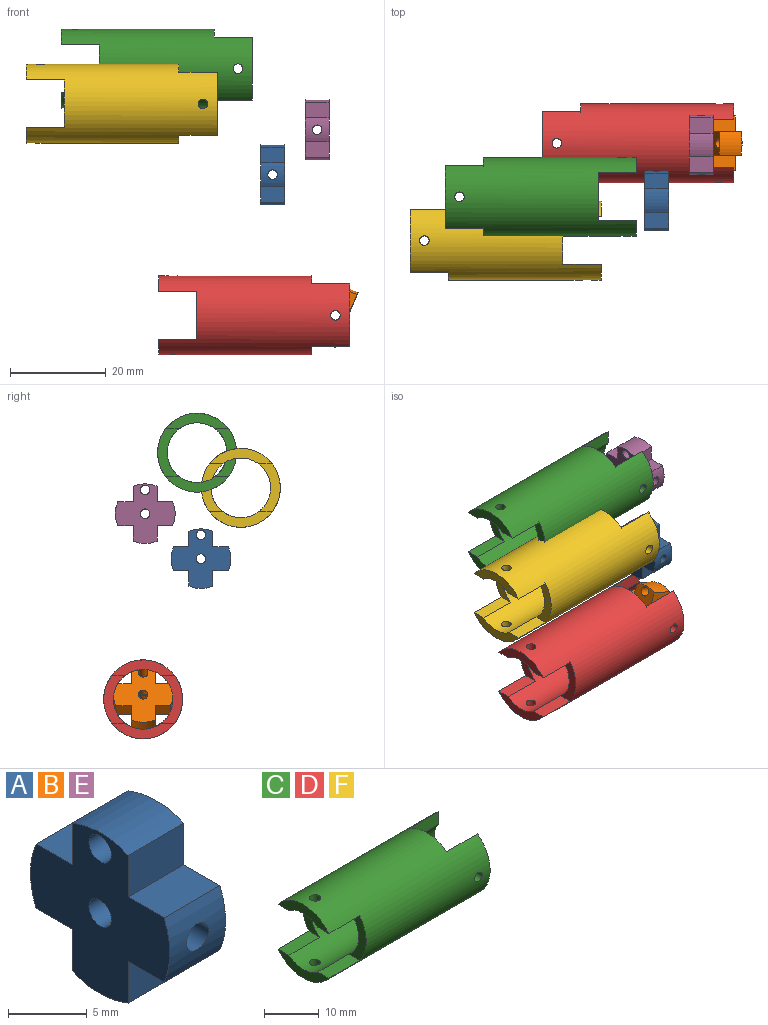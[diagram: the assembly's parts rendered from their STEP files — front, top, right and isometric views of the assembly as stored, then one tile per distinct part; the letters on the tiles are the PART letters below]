
ASSEMBLY  parts=6 mates=1
PART A: 19 faces, bbox 5x12.5x12.5 mm
  f0: cylinder r=1mm len=2.5mm, axis (-1,0,0), area 11.7mm2, adj f15,f17,f18
  f1: plane 5x3.23mm, normal (0,0,-1), area 16.1mm2, adj f2,f14,f15,f16
  f2: cylinder r=6.25mm len=5mm, axis (-1,0,0), area 22.6mm2, adj f1,f3,f15,f16,f17
  f3: plane 5x3.23mm, normal (0,0,1), area 16.1mm2, adj f2,f4,f15,f16
  f4: plane 5x3.23mm, normal (0,1,0), area 16.1mm2, adj f3,f5,f15,f16
  f5: cylinder r=6.25mm len=5mm, axis (-1,0,0), area 25.7mm2, adj f4,f6,f15,f16
  f6: plane 5x3.23mm, normal (0,-1,0), area 16.1mm2, adj f5,f7,f15,f16
  f7: plane 5x3.23mm, normal (0,0,1), area 16.1mm2, adj f6,f8,f15,f16
  f8: cylinder r=6.25mm len=5mm, axis (-1,0,0), area 22.6mm2, adj f7,f9,f15,f16,f18
  f9: plane 5x3.23mm, normal (0,0,-1), area 16.1mm2, adj f8,f10,f15,f16
  f10: plane 5x3.23mm, normal (0,-1,0), area 16.1mm2, adj f9,f11,f15,f16
  f11: cylinder r=6.25mm len=5mm, axis (-1,0,0), area 25.7mm2, adj f10,f14,f15,f16
  f12: cylinder r=1mm len=5mm, axis (-1,0,0), area 31.4mm2, adj f15,f16
  f13: cylinder r=1mm len=2.5mm, axis (-1,0,0), area 11.7mm2, adj f16,f17,f18
  f14: plane 5x3.23mm, normal (0,1,0), area 16.1mm2, adj f1,f11,f15,f16
  f15: plane 12.5x12.5mm, normal (1,0,0), area 90.3mm2, adj f0,f1,f2,f3,f4,f5,f6,f7
  f16: plane 12.5x12.5mm, normal (-1,0,0), area 90.3mm2, adj f1,f2,f3,f4,f5,f6,f7,f8
  f17: cylinder r=1mm len=6.25mm, axis (0,-1,0), area 35mm2, adj f0,f2,f13
  f18: cylinder r=1mm len=6.25mm, axis (0,-1,0), area 35mm2, adj f0,f8,f13
PART B: same geometry as A
PART C: 22 faces, bbox 40x16.5x16.5 mm
  f0: cylinder r=6.25mm len=40mm, axis (-1,0,0), area 1187.3mm2, adj f2,f3,f4,f5,f6,f7,f8,f9
  f1: cylinder r=8.25mm len=40mm, axis (-1,0,0), area 1717.1mm2, adj f2,f3,f4,f5,f6,f7,f8,f9
  f2: plane 13.12x3.25mm, normal (-1,0,0), area 23.4mm2, adj f0,f1,f14,f18
  f3: plane 13.12x3.25mm, normal (1,0,0), area 23.4mm2, adj f0,f1,f6,f10
  f4: plane 13.12x3.25mm, normal (1,0,0), area 23.4mm2, adj f0,f1,f7,f11
  f5: plane 13.12x3.25mm, normal (-1,0,0), area 23.4mm2, adj f0,f1,f15,f19
  f6: plane 8x2.81mm, normal (0,1,0), area 22.5mm2, adj f0,f1,f3,f8
  f7: plane 8x2.81mm, normal (0,-1,0), area 22.5mm2, adj f0,f1,f4,f8
  f8: plane 10x4.5mm, normal (1,0,0), area 22.2mm2, adj f0,f1,f6,f7
  f9: plane 10x4.5mm, normal (1,0,0), area 22.2mm2, adj f0,f1,f10,f11
  f10: plane 8x2.81mm, normal (0,1,0), area 22.5mm2, adj f0,f1,f3,f9
  f11: plane 8x2.81mm, normal (0,-1,0), area 22.5mm2, adj f0,f1,f4,f9
  f12: cylinder r=1mm len=2.08mm, axis (0,0,1), area 12.6mm2, adj f0,f1
  f13: cylinder r=1mm len=2.08mm, axis (0,0,1), area 12.6mm2, adj f0,f1
  f14: plane 8x2.81mm, normal (0,0,1), area 22.5mm2, adj f0,f1,f2,f16
  f15: plane 8x2.81mm, normal (0,0,-1), area 22.5mm2, adj f0,f1,f5,f16
  f16: plane 10x4.5mm, normal (-1,0,0), area 22.2mm2, adj f0,f1,f14,f15
  f17: plane 10x4.5mm, normal (-1,0,0), area 22.2mm2, adj f0,f1,f18,f19
  f18: plane 8x2.81mm, normal (0,0,1), area 22.5mm2, adj f0,f1,f2,f17
  f19: plane 8x2.81mm, normal (0,0,-1), area 22.5mm2, adj f0,f1,f5,f17
  f20: cylinder r=1mm len=2.08mm, axis (0,-1,0), area 12.6mm2, adj f0,f1
  f21: cylinder r=1mm len=2.08mm, axis (0,-1,0), area 12.6mm2, adj f0,f1
PART D: same geometry as C
PART E: same geometry as A
PART F: same geometry as C
PLACE A t=(38.63,11.37,-18.57)mm
PLACE B rot(axis=(0,1,0),22.8deg) t=(51.98,23.45,-47.02)mm
PLACE C t=(-3.11,12.17,3.63)mm
PLACE D t=(17.28,23.45,-47.99)mm fixed
PLACE E t=(47.95,23.03,-9.15)mm
PLACE F t=(-10.46,3.01,-3.74)mm
MATE cylindrical D.f20 <-> B.f17  axis (0,-1,0) through (54.28,15.19,-47.99)mm
